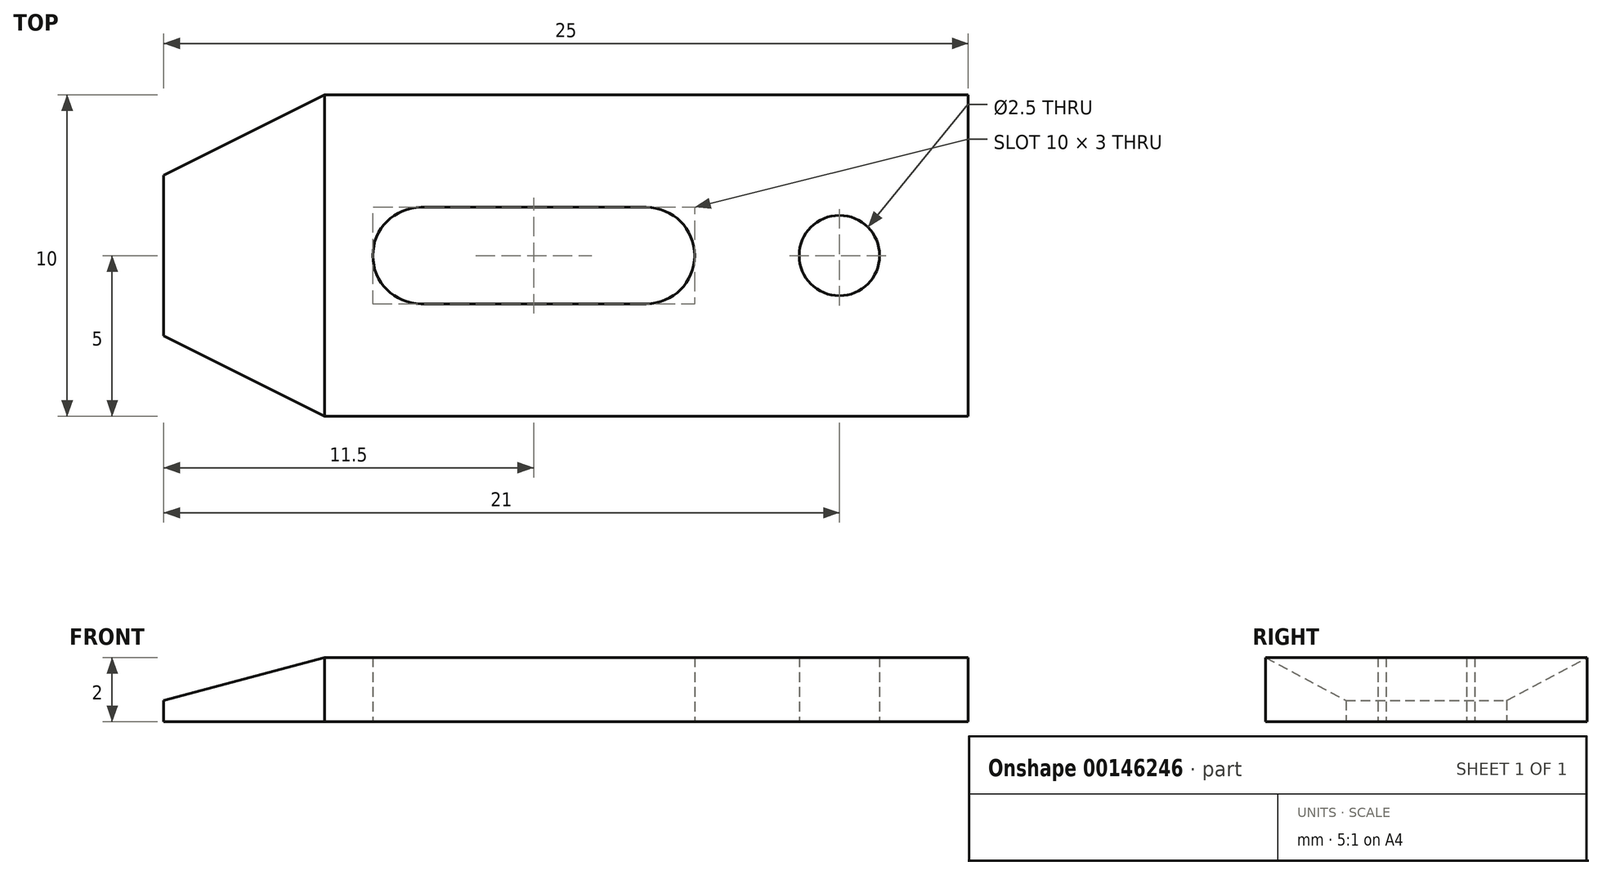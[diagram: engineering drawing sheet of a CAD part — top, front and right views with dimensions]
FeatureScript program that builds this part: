
annotation { "Feature Type Name" : "Feature", "Feature Type Description" : "" }
export const myFeature = defineFeature(function(context is Context, id is Id, definition is map)
    precondition{}
    {
        {
            var Q0;
            Q0=qCreatedBy(makeId("Top.planeOp"),FACE);
            var sketch = newSketch(context, id + "F0", { "sketchPlane" : qUnion([Q0])});
            skLineSegment(sketch, "E0.bottom", {"start": v(15, 5) * mm, "end": v(-5, 5) * mm});
            skLineSegment(sketch, "E0.top", {"start": v(15, -5) * mm, "end": v(-5, -5) * mm});
            skLineSegment(sketch, "E0.left", {"start": v(15, 5) * mm, "end": v(15, -5) * mm});
            skLineSegment(sketch, "E0.right", {"start": v(-10, 2.5) * mm, "end": v(-10, -2.5) * mm});
            skPoint(sketch, "E0.middle", {"position": v(0, 0) * mm});
            skLineSegment(sketch, "E1", {"start": v(-10, 2.5) * mm, "end": v(-5, 5) * mm});
            skLineSegment(sketch, "E2.MirrorCS", {"start": v(-10, -2.5) * mm, "end": v(-5, -5) * mm});
            skCircle(sketch, "E3", {"center": v(11, 0) * mm, "radius": 1.25 * mm});
            skArc(sketch, "E4", {"start": v(-2, 1.5) * mm, "mid": v(-3.5, 0) * mm, "end": v(-2, -1.5) * mm});
            skArc(sketch, "E5", {"start": v(5, -1.5) * mm, "mid": v(6.5, 0) * mm, "end": v(5, 1.5) * mm});
            skLineSegment(sketch, "E6", {"start": v(-2, 1.5) * mm, "end": v(5, 1.5) * mm});
            skLineSegment(sketch, "E7", {"start": v(-2, -1.5) * mm, "end": v(5, -1.5) * mm});
            skSolve(sketch);
        }
        {
            var Q0;
            Q0=makeQuery(id+"F0.imprint","IMPRINT",FACE,{"disambiguationData":[TD([[makeQuery(id+"F0.imprint","IMPRINT",EDGE,{"derivedFrom":sQuery(id+"F0.wireOp",EDGE,"E0.bottom")}),1.0]])]});
            extrude(context, id + "F1", {"entities" : qUnion([Q0]), "depth" : 2 * mm});
        }
        {
            var Q0;
            Q0=makeQuery(id+"F1.opExtrude","CAP_EDGE",EDGE,{"disambiguationData":[OSD([sQuery(id+"F0.wireOp",EDGE,"E0.right")])],"isStart":false});
            chamfer(context, id + "F2", {"entities" : qUnion([Q0]), "chamferType" : ChamferType.OFFSET_ANGLE, "width" : 5 * mm, "oppositeDirection" : false, "angle" : 15 * degree, "tangentPropagation" : true});
        }
    });
